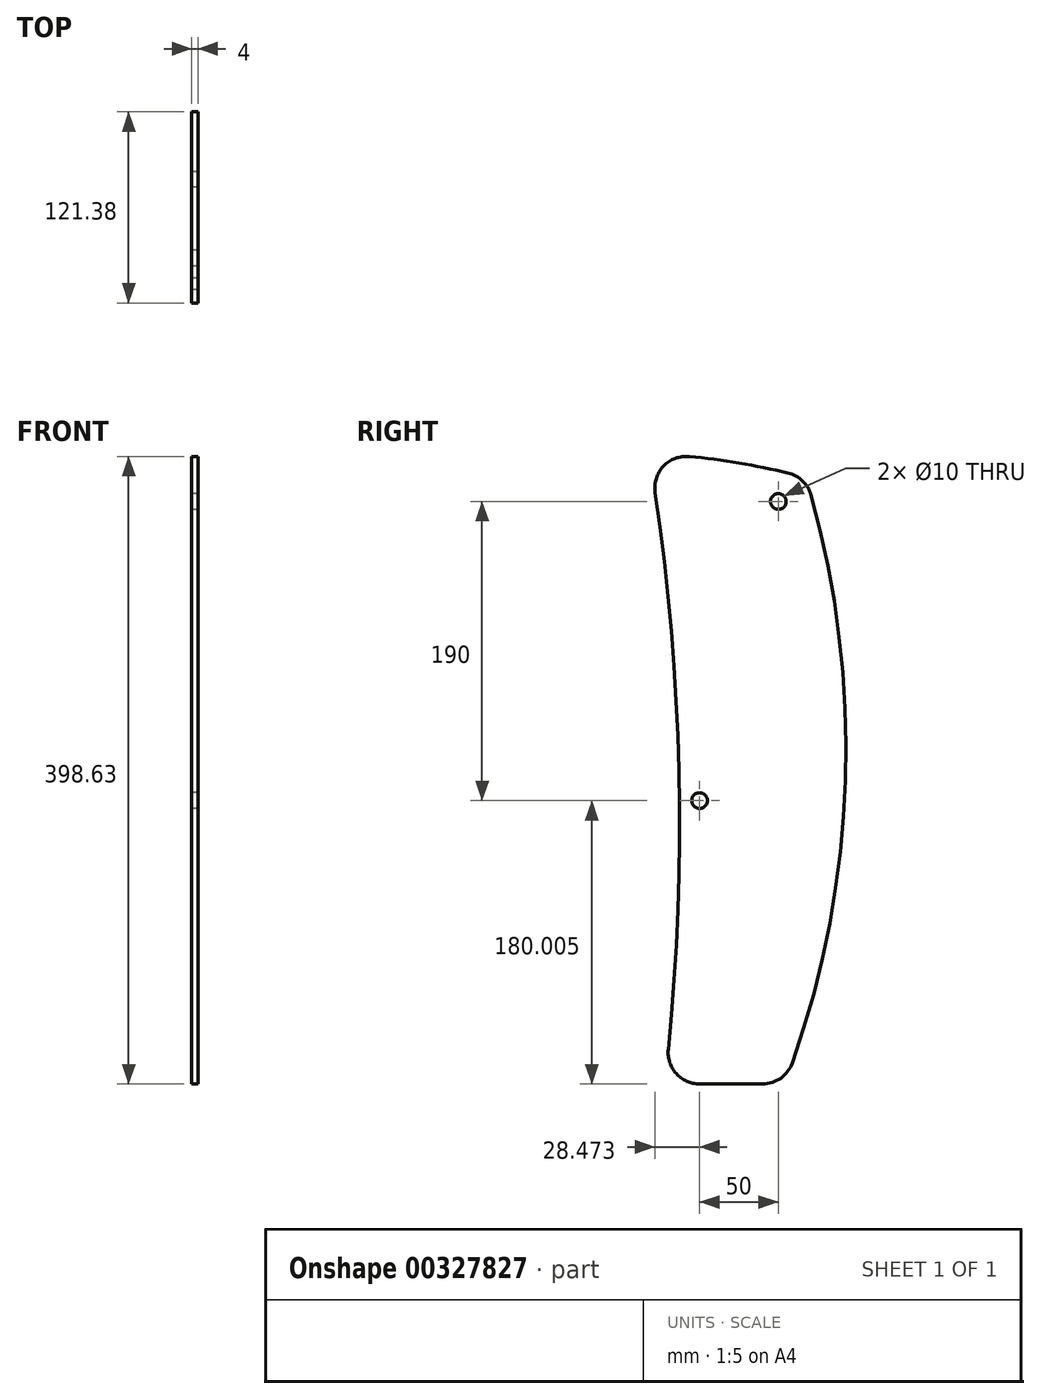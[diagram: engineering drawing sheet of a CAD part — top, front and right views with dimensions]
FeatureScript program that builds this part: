
annotation { "Feature Type Name" : "Feature", "Feature Type Description" : "" }
export const myFeature = defineFeature(function(context is Context, id is Id, definition is map)
    precondition{}
    {
        {
            var Q0;
            Q0=qCreatedBy(makeId("Right.planeOp"),FACE);
            var sketch = newSketch(context, id + "F0", { "sketchPlane" : qUnion([Q0])});
            skLineSegment(sketch, "E0.bottom", {"start": v(-93.5, -201.38) * mm, "end": v(36.5, -201.38) * mm});
            skLineSegment(sketch, "E0.top", {"start": v(-93.5, 198.62) * mm, "end": v(36.5, 198.62) * mm});
            skLineSegment(sketch, "E0.left", {"start": v(-93.5, -201.38) * mm, "end": v(-93.5, 198.62) * mm});
            skLineSegment(sketch, "E0.right", {"start": v(36.5, -201.38) * mm, "end": v(36.5, 198.62) * mm});
            skCircle(sketch, "E1", {"center": v(-63.5, -21.38) * mm, "radius": 5 * mm});
            skCircle(sketch, "E2", {"center": v(-13.5, 168.62) * mm, "radius": 5 * mm});
            skLineSegment(sketch, "E3", {"start": v(-63.5, -21.38) * mm, "end": v(-15.78, 249.23) * mm, "construction": true});
            skLineSegment(sketch, "E4.top", {"start": v(-93.5, -329.3) * mm, "end": v(36.5, -329.3) * mm, "construction": true});
            skLineSegment(sketch, "E4.left", {"start": v(-93.5, -201.38) * mm, "end": v(-93.5, -329.3) * mm, "construction": true});
            skLineSegment(sketch, "E4.right", {"start": v(36.5, -201.38) * mm, "end": v(36.5, -329.3) * mm, "construction": true});
            skLineSegment(sketch, "E5", {"start": v(-327.5, 87.29) * mm, "end": v(-327.5, -329.3) * mm});
            skSolve(sketch);
        }
        {
            var Q0;
            Q0 = qSketchRegion(id + "F0", true);
            extrude(context, id + "F1", {"entities" : qUnion([Q0]), "depth" : 4 * mm});
        }
        {
            var Q0;
            Q0=makeQuery(id+"F0.imprint","IMPRINT",FACE,{"disambiguationData":[TD([[makeQuery(id+"F0.imprint","IMPRINT",EDGE,{"derivedFrom":sQuery(id+"F0.wireOp",EDGE,"E0.bottom")}),1.0]])]});
            var sketch = newSketch(context, id + "F2", { "sketchPlane" : qUnion([Q0])});
            skArc(sketch, "E6", {"start": v(-83.4, -179.38) * mm, "mid": v(-76.66, -2.28) * mm, "end": v(-91.76, 174.32) * mm});
            skArc(sketch, "E7", {"start": v(-4.63, -188.02) * mm, "mid": v(29.08, -8.61) * mm, "end": v(7.29, 172.63) * mm});
            skArc(sketch, "E8", {"start": v(-7.3, 186.7) * mm, "mid": v(-38.5, 193.04) * mm, "end": v(-70.09, 197.16) * mm});
            skPoint(sketch, "E9.orphan", {"position": v(0, 196.75) * mm});
            skPoint(sketch, "E10.orphan", {"position": v(0, -174.33) * mm});
            skPoint(sketch, "E11.visualSharp", {"position": v(-10.38, -203.65) * mm});
            skArc(sketch, "E11.filletArc", {"start": v(-23.5, -201.38) * mm, "mid": v(-11.94, -197.7) * mm, "end": v(-4.63, -188.02) * mm});
            skPoint(sketch, "E12.visualSharp", {"position": v(4.05, 183.8) * mm});
            skArc(sketch, "E12.filletArc", {"start": v(7.29, 172.63) * mm, "mid": v(1.9, 181.64) * mm, "end": v(-7.3, 186.7) * mm});
            skPoint(sketch, "E13.visualSharp", {"position": v(-95.6, 198.84) * mm});
            skArc(sketch, "E13.filletArc", {"start": v(-70.09, 197.16) * mm, "mid": v(-86.48, 191.01) * mm, "end": v(-91.76, 174.32) * mm});
            skPoint(sketch, "E14.visualSharp", {"position": v(-89.2, -228.69) * mm});
            skArc(sketch, "E14.filletArc", {"start": v(-83.4, -179.38) * mm, "mid": v(-78.33, -194.8) * mm, "end": v(-63.5, -201.38) * mm});
            skLineSegment(sketch, "E15", {"start": v(-63.5, -201.38) * mm, "end": v(-23.5, -201.38) * mm});
            skSolve(sketch);
        }
        {
            var Q0;
            Q0 = qSketchRegion(id + "F2", true);
            extrude(context, id + "F3", {"entities" : qUnion([Q0]), "operationType" : NewBodyOperationType.INTERSECT, "depth" : 5 * mm, "offsetDistance" : 25 * mm});
        }
    });
